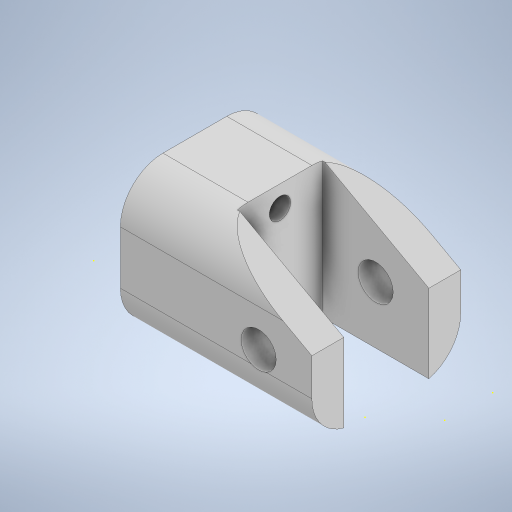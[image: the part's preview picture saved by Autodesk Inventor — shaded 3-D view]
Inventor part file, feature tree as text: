
AUTODESK INVENTOR PART (.ipt)
format: ipt  version: 2024 (Build 280153000, 153)  size: 646,144 bytes
history: native  units: mm
features: sketch x33, extrude x29, move_body x7, plane x4, split x4, boolean_combine x4, chamfer x3, fillet x1
ambient origin geometry x8: Origin, YZ Plane, XZ Plane, XY Plane, X Axis, Y Axis, Z Axis, Center Point
bodies: Solid1 (feature_tree), Solid2 (feature_tree), Solid3 (feature_tree), Solid6 (feature_tree), Solid7 (feature_tree), Solid8 (feature_tree), Solid9 (feature_tree), Solid10 (feature_tree), Solid11 (feature_tree)
feature tree (85):
  extrude  "Extrusion1"  Depth=16.0mm
  sketch  "Sketch2"  dims[d2=15.0mm d3=0.0mm d4=10.0mm]
  extrude  "Extrusion2"  Depth=10.0mm
  chamfer  "Chamfer1"  Distance=21.25mm
  extrude  "Extrusion3"  Depth=10.0mm TaperAngle=0.0deg
  extrude  "Extrusion4"  Depth=11.5mm TaperAngle=0.0deg
  extrude  "Extrusion5"  Depth=1.0mm TaperAngle=0.0deg
  chamfer  "Chamfer2"  Distance=6.0mm Angle=45.0deg
  sketch  "Sketch6"  dims[d14=7.0mm d15=11.5mm d16=0.0mm]
  extrude  "Extrusion6"  Depth=9.0mm
  extrude  "Extrusion7"  Depth=45.25mm TaperAngle=0.0deg
  chamfer  "Chamfer3"  Distance=11.5mm Angle=45.0deg
  sketch  "Sketch9"  dims[d26=3.3mm d27=45.25mm d28=0.0mm d29=11.5mm d30=5.5mm d31=45.0deg]
  extrude  "Extrusion8"  Depth=65.75mm TaperAngle=0.0deg
  extrude  "Extrusion9"  Depth=9.0mm TaperAngle=0.0deg
  extrude  "Extrusion10"  Depth=13.0mm TaperAngle=0.0deg
  sketch  "Sketch13"  dims[d43=24.0mm d44=21.0mm d45=0.0mm]
  extrude  "Extrusion11"  Depth=21.0mm TaperAngle=0.0deg
  extrude  "Extrusion12"  TaperAngle=0.0deg  [1 undecoded]
  extrude  "Extrusion13"  Depth=6.0mm TaperAngle=0.0deg
  plane  "Work Plane1"
  split  "Split1"
  move_body  "Move Body1"
  extrude  "Extrusion14"  Depth=0.5mm TaperAngle=0.0deg
  move_body  "Move Body2"
  extrude  "Extrusion15"  Depth=10.0mm
  sketch  "Sketch19"  dims[d70=31.0mm d71=29.5mm d72=0.0mm]
  sketch  "Sketch20"  dims[d74=11.0mm d75=1.0mm]
  extrude  "Extrusion16"  Depth=10.0mm
  extrude  "Extrusion18"  Depth=29.5mm TaperAngle=0.0deg
  extrude  "Extrusion19"  Depth=1.0mm
  extrude  "Extrusion20"  Depth=10.0mm TaperAngle=0.0deg
  boolean_combine  "Combine1"
  plane  "Work Plane3"
  split  "Split3"
  extrude  "Extrusion21"  TaperAngle=0.0deg  [1 undecoded]
  plane  "Work Plane4"
  split  "Split4"
  move_body  "Move Body3"
  move_body  "Move Body4"
  boolean_combine  "Combine3"
  extrude  "Extrusion22"  Depth=1.0mm TaperAngle=0.0deg
  extrude  "Extrusion23"  Depth=12.5mm TaperAngle=0.0deg
  extrude  "Extrusion24"  TaperAngle=0.0deg  [1 undecoded]
  extrude  "Extrusion25"  Depth=46.5mm TaperAngle=0.0deg
  move_body  "Move Body5"
  sketch  "Sketch32"  dims[d102=46.5mm d103=0.0mm d104=4.0mm d105=1.0mm]
  boolean_combine  "Combine4"
  extrude  "Extrusion26"  Depth=2.0mm
  extrude  "Extrusion27"  Depth=4.0mm
  fillet  "Fillet2"  Radius=1.0mm
  sketch  "Sketch34"  dims[d109=5.5mm d110=4.0mm d111=0.0mm d112=0.0mm]
  extrude  "Extrusion28"  Depth=46.5mm TaperAngle=0.0deg
  plane  "Work Plane5"
  split  "Split5"
  move_body  "Move Body6"
  extrude  "Extrusion29"  Depth=4.0mm TaperAngle=0.0deg
  move_body  "Move Body7"
  boolean_combine  "Combine5"
  extrude  "Extrusion30"  TaperAngle=0.0deg  [1 undecoded]
  sketch  "Sketch1"  dims[d0=36.0mm d1=16.0mm]
  sketch  "Sketch3"  dims[d5=10.0mm]
  sketch  "Sketch4"  dims[d6=3.3mm d7=21.25mm d8=0.0mm]
  sketch  "Sketch5"  dims[d9=10.0mm d10=5.5mm d11=45.0deg d12=10.0mm d13=0.0mm]
  sketch  "Sketch7"  dims[d17=3.3mm d18=1.0mm d19=0.0mm d20=6.0mm d21=11.5mm d22=45.0deg]
  sketch  "Sketch8"  dims[d23=15.0mm d24=0.0mm d25=9.0mm]
  sketch  "Sketch10"  dims[d32=2.0mm d33=65.75mm d34=0.0mm]
  sketch  "Sketch11"  dims[d35=0.5mm d36=0.0mm d37=9.0mm d38=0.0mm]
  sketch  "Sketch12"  dims[d39=0.5mm d40=0.0mm d41=13.0mm d42=0.0mm]
  sketch  "Sketch14"  dims[d46=12.25mm d47=-12.0mm d48=0.0mm d49=0.0mm]
  sketch  "Sketch15"  dims[d50=30.0mm d51=0.0mm d52=6.0mm d53=0.0mm d54=0.0mm]
  sketch  "Sketch16"  dims[d56=0.5mm d57=0.0mm d58=0.5mm d59=0.0mm]
  sketch  "Sketch17"  dims[d64=10.0mm d65=0.0mm d66=3.0mm]
  sketch  "Sketch18"  dims[d67=10.0mm d68=0.0mm d69=1.0mm]
  sketch  "Sketch22"  dims[d76=1.0mm d77=10.0mm d78=0.0mm]
  sketch  "Sketch25"  dims[d79=5.5mm d80=0.0mm d81=0.0mm d82=-1.0mm]
  sketch  "Sketch27"  dims[d83=0.0mm d84=0.0mm d85=1.0mm d86=1.0mm d87=0.0mm]
  sketch  "Sketch28"  dims[d88=1.0mm d89=0.0mm d90=12.5mm d91=0.0mm]
  sketch  "Sketch29"  dims[d92=19.0mm d93=0.0mm d94=-12.0mm d95=0.0mm d96=0.0mm]
  sketch  "Sketch30"  dims[d97=2.0mm d98=46.5mm d99=0.0mm]
  sketch  "Sketch31"  dims[d100=2.0mm d101=2.0mm]
  sketch  "Sketch33"  dims[d106=19.0mm d107=46.5mm d108=0.0mm]
  sketch  "Sketch35"  dims[d113=7.0mm d114=0.0mm d115=-8.0mm d116=0.0mm d117=0.0mm]
  sketch  "Sketch36"  dims[d118=7.0mm]
  sketch  "Sketch37"  dims[d119=19.75mm d120=0.0mm]
note: 4 required parameter values undecoded (feature->parameter linkage not recoverable at this tier; creation-order binding heuristic only, values carry confidence <= 0.55)
